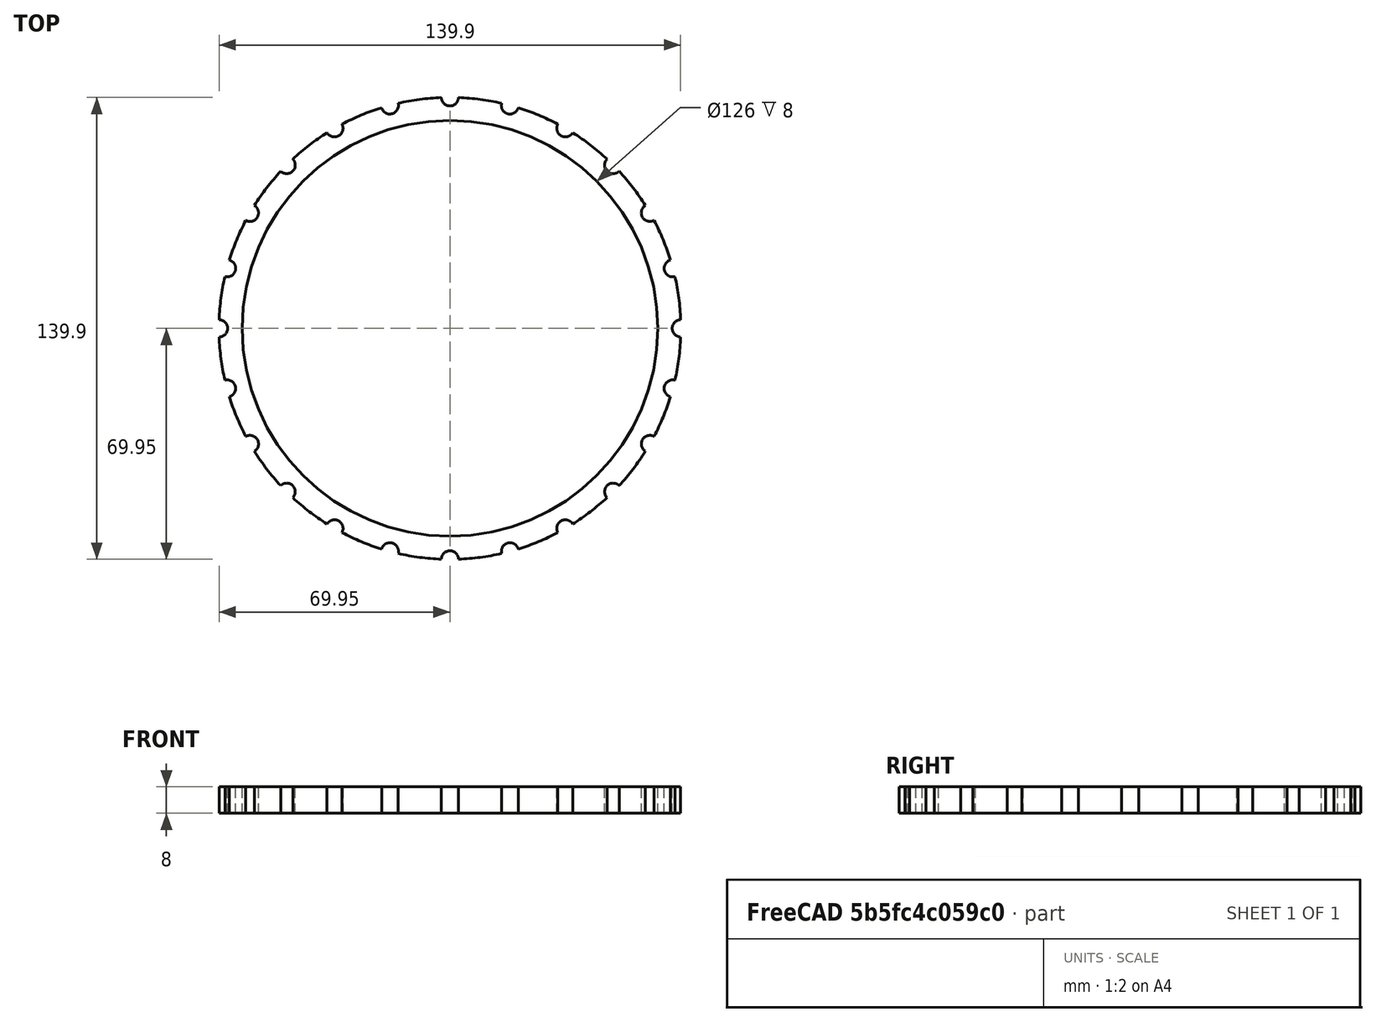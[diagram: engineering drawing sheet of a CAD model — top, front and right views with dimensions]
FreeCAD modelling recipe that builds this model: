
FCSTD DOCUMENT
Label: rat.social.top
objects: Part::Cylinder×9, Part::Mirroring×5, Part::Cut×2, Part::MultiFuse×2
note: 18 computed .brp shape members not serialized (recipe doc carries the construction recipe); baked Part::Feature solids carry a one-line shape summary decoded from their .brp

FEATURE [Part::Cylinder] Cylinder
  Angle = 360
  Height = 8
  Radius = 70
FEATURE [Part::Cylinder] Cylinder001  label="pole1"
  Angle = 360
  Height = 20
  Placement = pos=(70,0,0) rot=(0,0,1;0rad)
  Radius = 2.6
FEATURE [Part::Cylinder] Cylinder002
  Angle = 360
  Height = 10
  Radius = 63
FEATURE [Part::Cut] Cut
  Base = -> Cylinder
  Tool = -> Cylinder002
FEATURE [Part::Cylinder] Cylinder001001
  Angle = 360
  Height = 20
  Placement = pos=(0,70,0) rot=(0,0,1;0rad)
  Radius = 2.6
FEATURE [Part::Cylinder] Cylinder001002
  Angle = 360
  Height = 20
  Placement = pos=(18.2,67.55,0) rot=(0,0,1;0rad)
  Radius = 2.6
FEATURE [Part::Cylinder] Cylinder001002001  label="pole2"
  Angle = 360
  Height = 20
  Placement = pos=(67.55,18.2,0) rot=(0,0,1;0rad)
  Radius = 2.6
FEATURE [Part::Cylinder] Cylinder001002001001  label="pole003"
  Angle = 360
  Height = 20
  Placement = pos=(60.62,35,0) rot=(0,0,1;0rad)
  Radius = 2.6
FEATURE [Part::Cylinder] Cylinder001002001001001  label="pole004"
  Angle = 360
  Height = 20
  Placement = pos=(49.49,49.49,0) rot=(0,0,1;0rad)
  Radius = 2.6
FEATURE [Part::Cylinder] Cylinder001002001001001001  label="pole005"
  Angle = 360
  Height = 26
  Placement = pos=(35,60.62,0) rot=(0,0,1;0rad)
  Radius = 2.6
FEATURE [Part::MultiFuse] Fusion
  Shapes = -> [Cylinder001002001,Cylinder001002001001,Cylinder001002001001001,Cylinder001002001001001001,Cylinder001002]
FEATURE [Part::Mirroring] Part__Mirroring  label="Fusion (Mirror #1)"
  Base = (42.875,1.90735e-06,13)
  Normal = (0,1,-1.19209e-07)
  Placement = pos=(0,0,-5) rot=(0,0,1;0rad)
  Source = -> Fusion
FEATURE [Part::Mirroring] Part__Mirroring001  label="Fusion (Mirror #2)"
  Base = (2.86102e-06,42.7668,16)
  Normal = (1,0,-1.19209e-07)
  Placement = pos=(0,0,-2) rot=(0,0,1;0rad)
  Source = -> Fusion
FEATURE [Part::Mirroring] Part__Mirroring002  label="Fusion (Mirror #3)"
  Base = (0,0,0)
  Normal = (1,0,0)
  Placement = pos=(0,0,-4) rot=(0,0,1;0rad)
  Source = -> Part__Mirroring
FEATURE [Part::Mirroring] Part__Mirroring003  label="pole1 (Mirror #4)"
  Base = (0,0,0)
  Normal = (1,0,0)
  Placement = pos=(0,0,-3) rot=(0,0,1;0rad)
  Source = -> Cylinder001
FEATURE [Part::Mirroring] Part__Mirroring004  label="Cylinder001001 (Mirror #5)"
  Base = (0,0,0)
  Normal = (0,1,0)
  Placement = pos=(0,0,-4) rot=(0,0,1;0rad)
  Source = -> Cylinder001001
FEATURE [Part::MultiFuse] Fusion001
  Shapes = -> [Cylinder001002,Cylinder001002001,Part__Mirroring001,Cylinder001001,Cylinder001002001001001001,Part__Mirroring003,Part__Mirroring,Fusion,Part__Mirroring004,Cylinder001002001001,Cylinder001,Part__Mirroring002,Cylinder001002001001001]
FEATURE [Part::Cut] Cut001
  Base = -> Cut
  Tool = -> Fusion001
